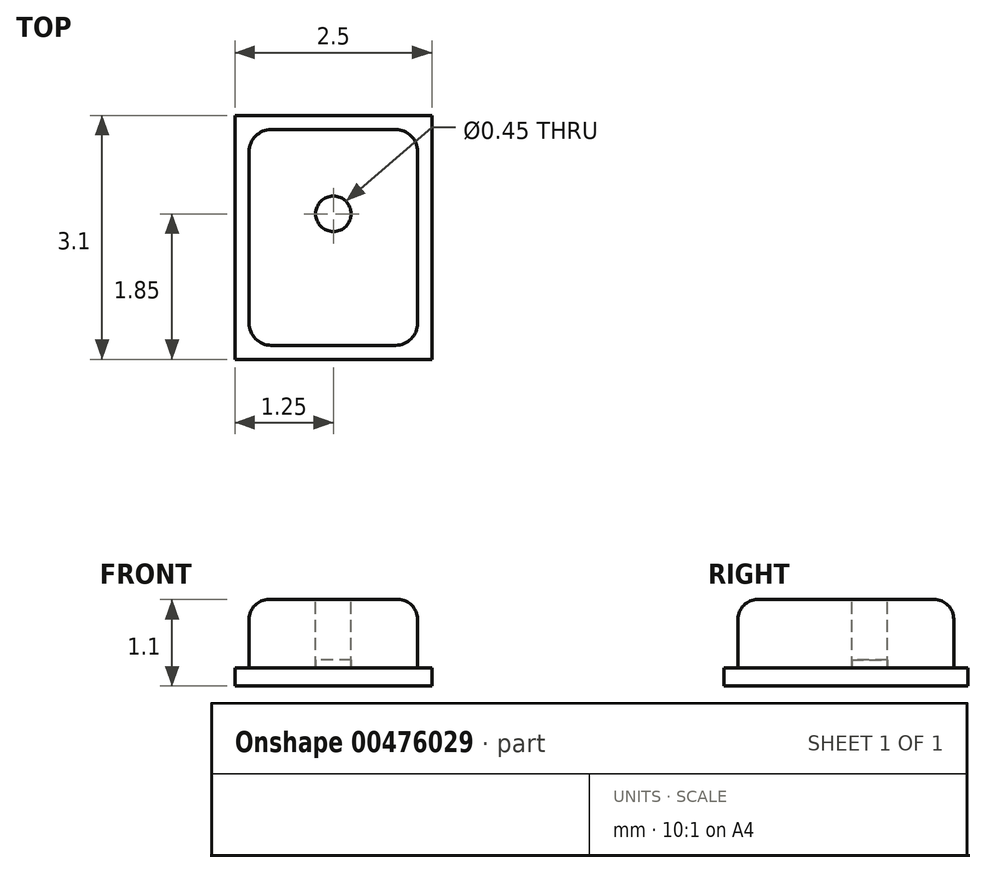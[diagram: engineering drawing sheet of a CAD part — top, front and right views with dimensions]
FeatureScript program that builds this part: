
annotation { "Feature Type Name" : "Feature", "Feature Type Description" : "" }
export const myFeature = defineFeature(function(context is Context, id is Id, definition is map)
    precondition{}
    {
        {
            var Q0;
            Q0=qCreatedBy(makeId("Top.planeOp"),FACE);
            var sketch = newSketch(context, id + "F0", { "sketchPlane" : qUnion([Q0])});
            skLineSegment(sketch, "E0.bottom", {"start": v(1.25, -1.55) * mm, "end": v(-1.25, -1.55) * mm});
            skLineSegment(sketch, "E0.top", {"start": v(1.25, 1.55) * mm, "end": v(-1.25, 1.55) * mm});
            skLineSegment(sketch, "E0.left", {"start": v(1.25, -1.55) * mm, "end": v(1.25, 1.55) * mm});
            skLineSegment(sketch, "E0.right", {"start": v(-1.25, -1.55) * mm, "end": v(-1.25, 1.55) * mm});
            skPoint(sketch, "E0.middle", {"position": v(0, 0) * mm});
            skSolve(sketch);
        }
        {
            var Q0;
            Q0 = qSketchRegion(id + "F0", true);
            extrude(context, id + "F1", {"entities" : qUnion([Q0]), "depth" : .23 * mm});
        }
        {
            var Q0;
            Q0=makeQuery(id+"F1.opExtrude","CAP_FACE",FACE,{"disambiguationData":[OSD([sQuery(id+"F0.wireOp",EDGE,"E0.bottom"),sQuery(id+"F0.wireOp",EDGE,"E0.top"),sQuery(id+"F0.wireOp",EDGE,"E0.left"),sQuery(id+"F0.wireOp",EDGE,"E0.right")])],"isStart":false});
            var sketch = newSketch(context, id + "F2", { "sketchPlane" : qUnion([Q0])});
            skLineSegment(sketch, "E1.bottom", {"start": v(0.79, -1.37) * mm, "end": v(-0.79, -1.37) * mm});
            skLineSegment(sketch, "E1.top", {"start": v(0.79, 1.37) * mm, "end": v(-0.79, 1.37) * mm});
            skLineSegment(sketch, "E1.left", {"start": v(1.07, -1.09) * mm, "end": v(1.07, 1.09) * mm});
            skLineSegment(sketch, "E1.right", {"start": v(-1.07, -1.09) * mm, "end": v(-1.07, 1.09) * mm});
            skPoint(sketch, "E1.middle", {"position": v(0, 0) * mm});
            skPoint(sketch, "E2.visualSharp", {"position": v(-1.07, 1.37) * mm});
            skArc(sketch, "E2.filletArc", {"start": v(-0.79, 1.37) * mm, "mid": v(-0.99, 1.29) * mm, "end": v(-1.07, 1.09) * mm});
            skPoint(sketch, "E3.visualSharp", {"position": v(1.07, 1.37) * mm});
            skArc(sketch, "E3.filletArc", {"start": v(1.07, 1.09) * mm, "mid": v(0.99, 1.29) * mm, "end": v(0.79, 1.37) * mm});
            skPoint(sketch, "E4.visualSharp", {"position": v(1.07, -1.37) * mm});
            skArc(sketch, "E4.filletArc", {"start": v(0.79, -1.37) * mm, "mid": v(0.99, -1.29) * mm, "end": v(1.07, -1.09) * mm});
            skPoint(sketch, "E5.visualSharp", {"position": v(-1.07, -1.37) * mm});
            skArc(sketch, "E5.filletArc", {"start": v(-1.07, -1.1) * mm, "mid": v(-0.99, -1.29) * mm, "end": v(-0.79, -1.37) * mm});
            skSolve(sketch);
        }
        {
            var Q0;
            Q0 = qSketchRegion(id + "F2", true);
            extrude(context, id + "F3", {"entities" : qUnion([Q0]), "depth" : (1.1 - .23) * mm});
        }
        {
            var Q0;
            Q0=makeQuery(id+"F3.opExtrude","CAP_EDGE",EDGE,{"disambiguationData":[OSD([sQuery(id+"F2.wireOp",EDGE,"E1.bottom")])],"isStart":false});
            fillet(context, id + "F4", {"entities" : qUnion([Q0]), "radius" : .25 * mm, "tangentPropagation" : true, "allowEdgeOverflow" : false});
        }
        {
            var Q0;
            Q0=makeQuery(id+"F3.opExtrude","CAP_FACE",FACE,{"disambiguationData":[OSD([sQuery(id+"F2.wireOp",EDGE,"E1.bottom"),sQuery(id+"F2.wireOp",EDGE,"E1.top"),sQuery(id+"F2.wireOp",EDGE,"E1.left"),sQuery(id+"F2.wireOp",EDGE,"E1.right"),sQuery(id+"F2.wireOp",EDGE,"E2.filletArc"),sQuery(id+"F2.wireOp",EDGE,"E3.filletArc"),sQuery(id+"F2.wireOp",EDGE,"E4.filletArc"),sQuery(id+"F2.wireOp",EDGE,"E5.filletArc")])],"isStart":false});
            var sketch = newSketch(context, id + "F5", { "sketchPlane" : qUnion([Q0])});
            skCircle(sketch, "E6", {"center": v(0, 0.3) * mm, "radius": 0.23 * mm});
            skSolve(sketch);
        }
        {
            var Q0;
            Q0 = qSketchRegion(id + "F5", true);
            var Q1;
            Q1=makeQuery(id+"F1.opExtrude","CAP_FACE",FACE,{"disambiguationData":[OSD([sQuery(id+"F0.wireOp",EDGE,"E0.bottom"),sQuery(id+"F0.wireOp",EDGE,"E0.top"),sQuery(id+"F0.wireOp",EDGE,"E0.left"),sQuery(id+"F0.wireOp",EDGE,"E0.right")])],"isStart":false});
            extrude(context, id + "F6", {"entities" : qUnion([Q0]), "operationType" : NewBodyOperationType.REMOVE, "endBound" : BoundingType.UP_TO_SURFACE, "oppositeDirection" : true, "endBoundEntityFace" : qUnion([Q1]), "depth" : 25 * mm});
        }
        {
            var Q0;
            Q0=makeQuery(id+"F1.opExtrude","CAP_FACE",FACE,{"disambiguationData":[OSD([sQuery(id+"F0.wireOp",EDGE,"E0.bottom"),sQuery(id+"F0.wireOp",EDGE,"E0.top"),sQuery(id+"F0.wireOp",EDGE,"E0.left"),sQuery(id+"F0.wireOp",EDGE,"E0.right")])],"isStart":false});
            var sketch = newSketch(context, id + "F7", { "sketchPlane" : qUnion([Q0])});
            skCircle(sketch, "E7", {"center": v(0, 0.3) * mm, "radius": 0.23 * mm});
            skSolve(sketch);
        }
        {
            var Q0;
            Q0 = qSketchRegion(id + "F7", true);
            extrude(context, id + "F8", {"entities" : qUnion([Q0]), "depth" : .1 * mm});
        }
    });
